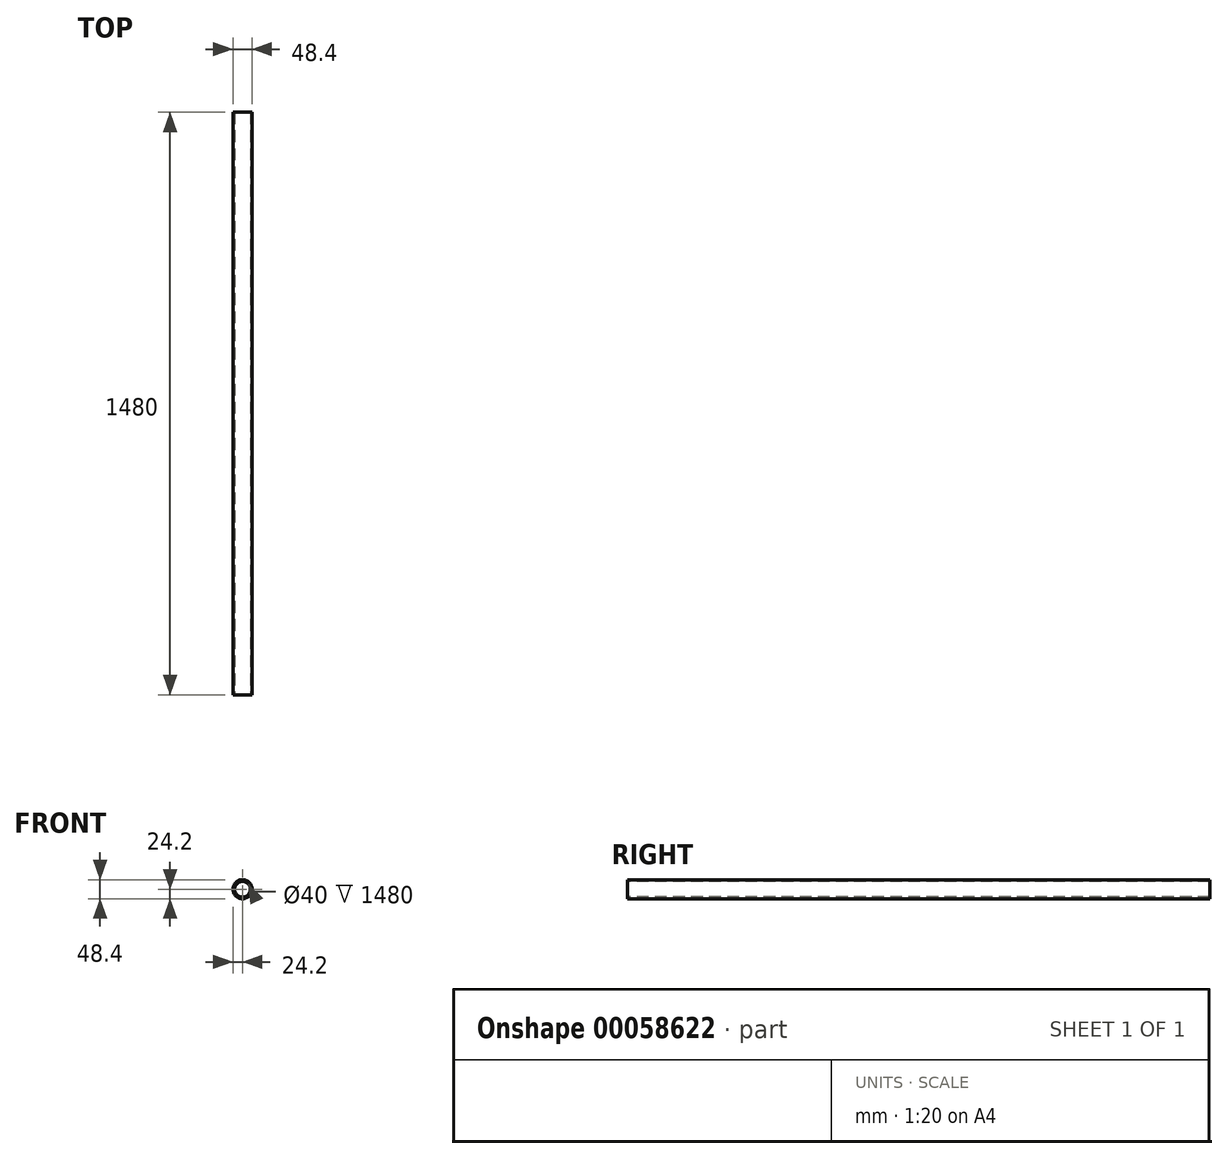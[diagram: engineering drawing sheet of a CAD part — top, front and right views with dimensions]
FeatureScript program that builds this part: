
annotation { "Feature Type Name" : "Feature", "Feature Type Description" : "" }
export const myFeature = defineFeature(function(context is Context, id is Id, definition is map)
    precondition{}
    {
        {
            var Q0;
            Q0=qCreatedBy(makeId("Front.planeOp"),FACE);
            var sketch = newSketch(context, id + "F0", { "sketchPlane" : qUnion([Q0])});
            skCircle(sketch, "E0", {"center": v(0, 0) * mm, "radius": 24.2 * mm});
            skCircle(sketch, "E1", {"center": v(0, 0) * mm, "radius": 20 * mm});
            skSolve(sketch);
        }
        {
            var Q0;
            Q0 = qSketchRegion(id + "F0", true);
            extrude(context, id + "F1", {"entities" : qUnion([Q0]), "oppositeDirection" : true, "depth" : 1480 * mm});
        }
    });
